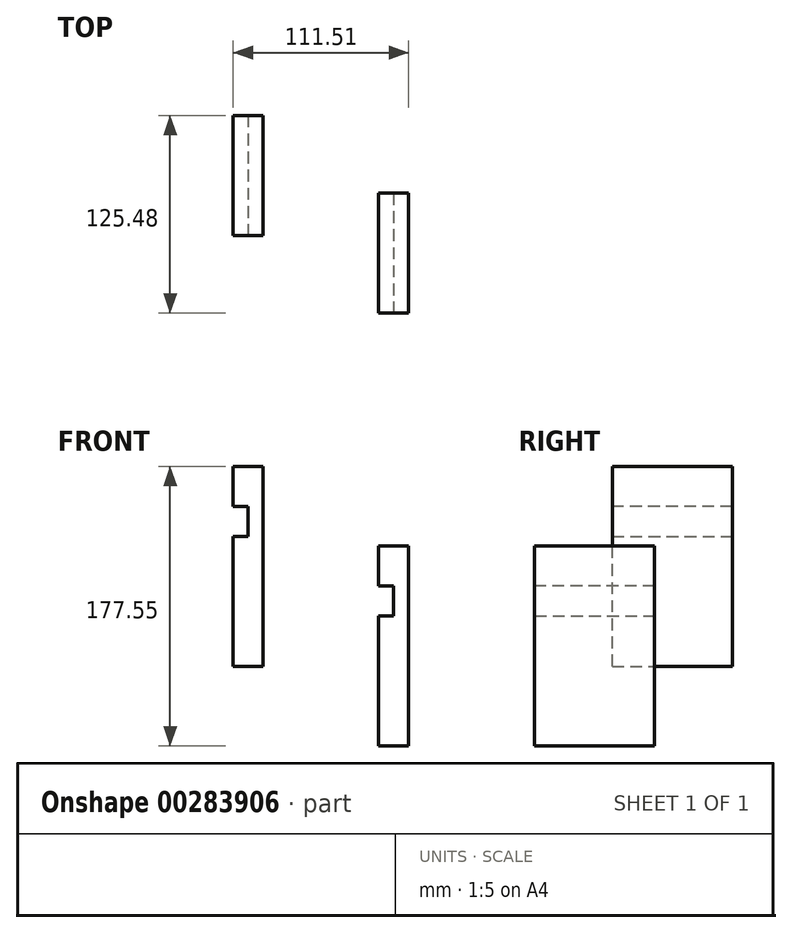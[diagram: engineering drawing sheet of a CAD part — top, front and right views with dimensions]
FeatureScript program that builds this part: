
annotation { "Feature Type Name" : "Feature", "Feature Type Description" : "" }
export const myFeature = defineFeature(function(context is Context, id is Id, definition is map)
    precondition{}
    {
        {
            var Q0;
            Q0=qCreatedBy(makeId("Front.planeOp"),FACE);
            var sketch = newSketch(context, id + "F0", { "sketchPlane" : qUnion([Q0])});
            skLineSegment(sketch, "E0.bottom", {"start": v(0, 0) * mm, "end": v(-19.05, 0) * mm});
            skLineSegment(sketch, "E0.top", {"start": v(0, 127) * mm, "end": v(-19.05, 127) * mm});
            skLineSegment(sketch, "E0.left", {"start": v(0, 0) * mm, "end": v(0, 127) * mm});
            skLineSegment(sketch, "E0.right", {"start": v(-19.05, 0) * mm, "end": v(-19.05, 127) * mm});
            skSolve(sketch);
        }
        {
            var Q0;
            Q0 = qSketchRegion(id + "F0", true);
            extrude(context, id + "F1", {"entities" : qUnion([Q0]), "depth" : 76.2 * mm});
        }
        {
            var Q0;
            Q0=makeQuery(id+"F1.opExtrude","CAP_FACE",FACE,{"disambiguationData":[OSD([sQuery(id+"F0.wireOp",EDGE,"E0.bottom"),sQuery(id+"F0.wireOp",EDGE,"E0.top"),sQuery(id+"F0.wireOp",EDGE,"E0.left"),sQuery(id+"F0.wireOp",EDGE,"E0.right")])],"isStart":false});
            var sketch = newSketch(context, id + "F2", { "sketchPlane" : qUnion([Q0])});
            skSolve(sketch);
        }
        {
            var Q0;
            Q0=makeQuery(id+"F2.imprint","IMPRINT",FACE,{"disambiguationData":[TD([[makeQuery(id+"F2.imprint","IMPRINT",EDGE,{"derivedFrom":makeQuery(id+"F1.opExtrude","CAP_EDGE",EDGE,{"disambiguationData":[OSD([sQuery(id+"F0.wireOp",EDGE,"E0.bottom")])],"isStart":false})}),-1.0]])]});
            var sketch = newSketch(context, id + "F3", { "sketchPlane" : qUnion([Q0])});
            skLineSegment(sketch, "E1", {"start": v(-19.16, 127) * mm, "end": v(-19.16, 101.6) * mm});
            skLineSegment(sketch, "E2", {"start": v(-19.16, 101.6) * mm, "end": v(-9.64, 101.6) * mm});
            skLineSegment(sketch, "E3", {"start": v(-9.64, 101.6) * mm, "end": v(-9.64, 82.55) * mm});
            skLineSegment(sketch, "E4", {"start": v(-9.64, 82.55) * mm, "end": v(-19.16, 82.55) * mm});
            skLineSegment(sketch, "E5", {"start": v(-19.16, 82.55) * mm, "end": v(-19.16, 101.6) * mm});
            skSolve(sketch);
        }
        {
            var Q0;
            Q0 = qSketchRegion(id + "F3", true);
            extrude(context, id + "F4", {"entities" : qUnion([Q0]), "operationType" : NewBodyOperationType.REMOVE, "oppositeDirection" : true, "depth" : 101.6 * mm});
        }
        {
            var Q0;
            Q0=makeQuery(id+"F1.opExtrude","SWEPT_BODY",BODY,{"disambiguationData":[OSD([sQuery(id+"F0.wireOp",EDGE,"E0.bottom"),sQuery(id+"F0.wireOp",EDGE,"E0.top"),sQuery(id+"F0.wireOp",EDGE,"E0.left"),sQuery(id+"F0.wireOp",EDGE,"E0.right")])]});
            transform(context, id + "F5", {"entities" : qUnion([Q0]), "transformType" : TransformType.TRANSLATION_3D, "dx" : -92.46 * mm, "dy" : 49.28 * mm, "dz" : 50.55 * mm, "makeCopy" : true});
        }
    });
